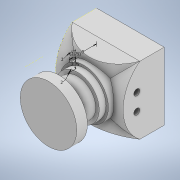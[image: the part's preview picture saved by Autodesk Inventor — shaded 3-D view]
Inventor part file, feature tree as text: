
AUTODESK INVENTOR PART (.ipt)
format: ipt  version: 2020 (Build 240168000, 168)  size: 225,280 bytes
history: native  units: in
note: dims shown in document units (in); Inventor stores cm internally (conversion verified against a paired STEP export)
features: sketch x11, extrude x9, projected_geometry x7, plane x1
ambient origin geometry x8: Origin, YZ Plane, XZ Plane, XY Plane, X Axis, Y Axis, Z Axis, Center Point
bodies: Solid1 (feature_tree)
feature tree (28):
  extrude  "Extrusion1"  Depth=0.874in
  extrude  "Extrusion2"  Depth=0.315in
  sketch  "Sketch3"  dims[d5=0.2854in d6=0.0in d9=0.2165in]
  extrude  "Extrusion4"  Depth=0.2165in
  extrude  "Extrusion5"  Depth=0.0886in
  extrude  "Extrusion6"  Depth=0.374in
  extrude  "Extrusion8"  Depth=0.0886in TaperAngle=0.0deg
  extrude  "Extrusion9"  Depth=0.2362in TaperAngle=0.0deg
  extrude  "Extrusion10"  Depth=0.1378in TaperAngle=0.0deg
  sketch  "Sketch12"  dims[d41=0.4409in]
  plane  "Work Plane2"
  extrude  "Extrusion12"  Depth=0.0394in
  sketch  "Sketch1"  dims[d0=0.874in d1=0.874in]
  sketch  "Sketch2"  dims[d2=0.315in d3=0.0in d4=0.6299in]
  projected_geometry  "Projected Loop1"
  sketch  "Sketch5"  dims[d10=0.0886in d11=0.0in d12=0.2165in]
  projected_geometry  "Projected Loop3"
  sketch  "Sketch6"  dims[d13=0.0886in d14=0.0in d15=0.374in]
  projected_geometry  "Projected Loop4"
  sketch  "Sketch7"  dims[d16=0.0886in d17=0.0in d23=0.0886in d24=0.0in]
  projected_geometry  "Projected Loop5"
  sketch  "Sketch9"  dims[d25=0.0787in d26=0.2362in d27=0.0in]
  projected_geometry  "Projected Loop8"
  sketch  "Sketch10"  dims[d28=0.7307in d29=0.1378in d30=0.0in]
  projected_geometry  "Projected Loop9"
  sketch  "Sketch11"  dims[d31=1.063in d36=0.0394in]
  sketch  "Sketch17"  dims[d48=0.3543in d49=0.1083in d50=0.0787in d52=0.1083in d53=0.0787in d54=0.0in d55=0.0in]
  projected_geometry  "Projected Loop11"
